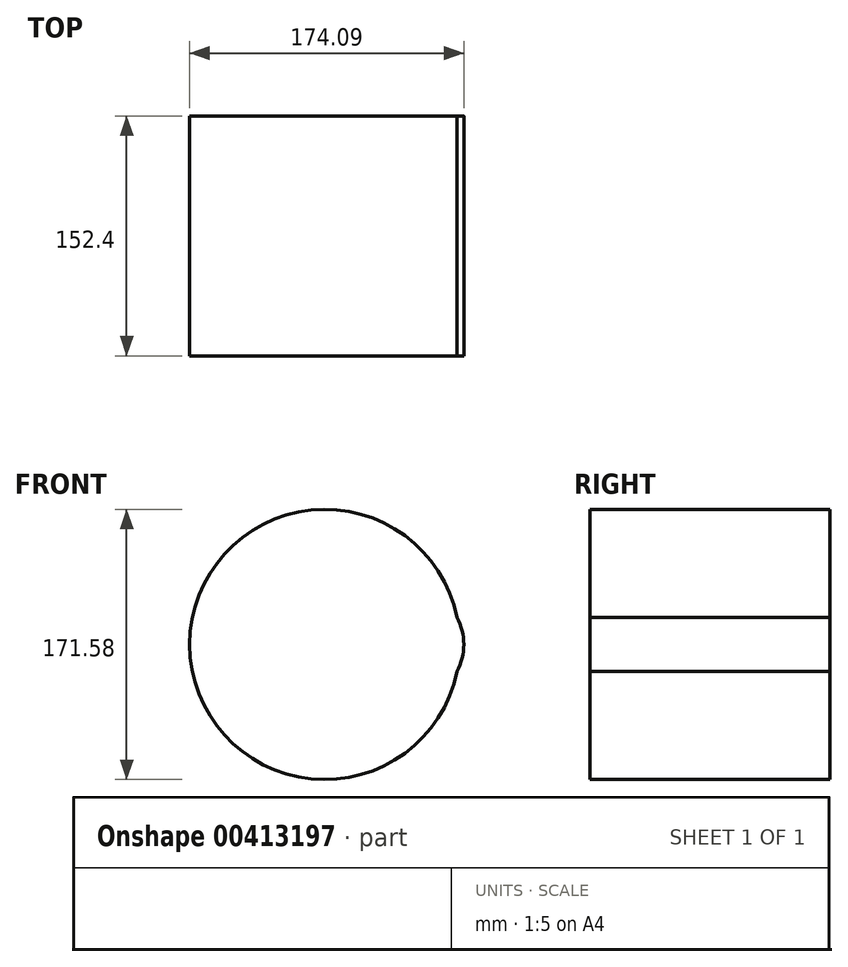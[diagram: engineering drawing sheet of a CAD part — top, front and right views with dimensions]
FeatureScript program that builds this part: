
annotation { "Feature Type Name" : "Feature", "Feature Type Description" : "" }
export const myFeature = defineFeature(function(context is Context, id is Id, definition is map)
    precondition{}
    {
        {
            var Q0;
            Q0=qCreatedBy(makeId("Front.planeOp"),FACE);
            var sketch = newSketch(context, id + "F0", { "sketchPlane" : qUnion([Q0])});
            skCircle(sketch, "E0", {"center": v(0, 0) * mm, "radius": 85.8 * mm});
            skCircle(sketch, "E1", {"center": v(51.46, 0) * mm, "radius": 36.84 * mm});
            skSolve(sketch);
        }
        {
            var Q0;
            Q0 = qSketchRegion(id + "F0", true);
            extrude(context, id + "F1", {"entities" : qUnion([Q0]), "depth" : 152.4 * mm});
        }
        {
            var Q0;
            Q0=makeQuery(id+"F1.opExtrude","CAP_FACE",FACE,{"disambiguationData":[OSD([sQuery(id+"F0.wireOp",EDGE,"E0"),sQuery(id+"F0.wireOp",EDGE,"E1")])],"isStart":false});
            var sketch = newSketch(context, id + "F2", { "sketchPlane" : qUnion([Q0])});
            skCircle(sketch, "E2", {"center": v(0, 0) * mm, "radius": 79.04 * mm});
            skSolve(sketch);
        }
        {
            var Q0;
            Q0=makeQuery(id+"F2.imprint","IMPRINT",FACE,{"disambiguationData":[TD([[makeQuery(id+"F2.imprint","IMPRINT",EDGE,{"derivedFrom":sQuery(id+"F2.wireOp",EDGE,"E2")}),1.0]])]});
            extrude(context, id + "F3", {"entities" : qUnion([Q0]), "operationType" : NewBodyOperationType.ADD, "oppositeDirection" : true, "depth" : 152.4 * mm});
        }
    });
